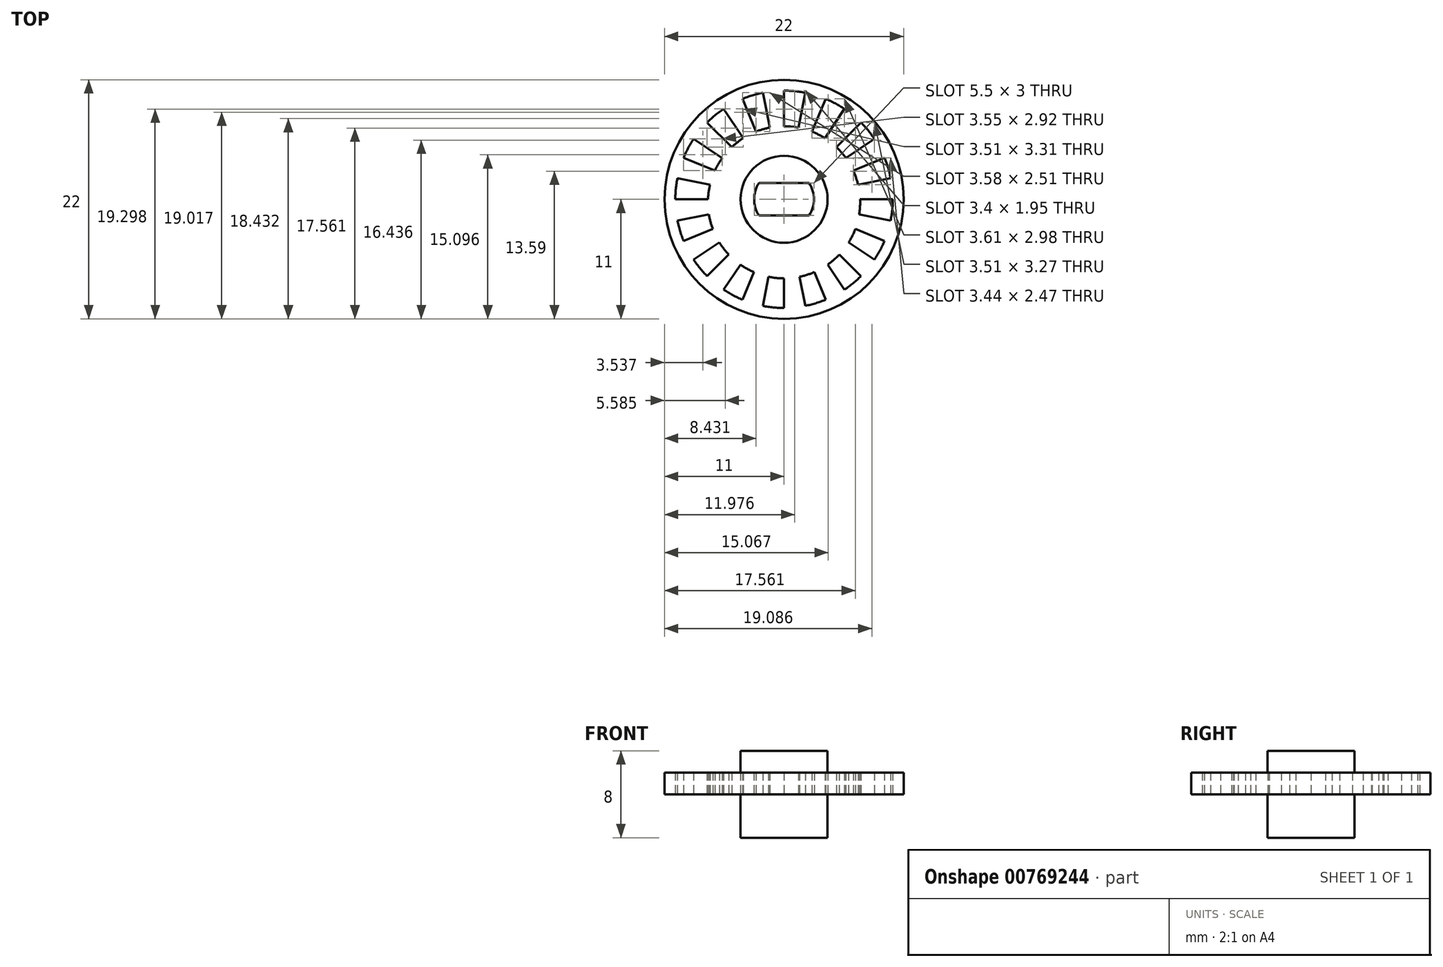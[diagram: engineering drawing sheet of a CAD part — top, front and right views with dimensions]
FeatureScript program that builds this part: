
annotation { "Feature Type Name" : "Feature", "Feature Type Description" : "" }
export const myFeature = defineFeature(function(context is Context, id is Id, definition is map)
    precondition{}
    {
        {
            var Q0;
            Q0=qCreatedBy(makeId("Top.planeOp"),FACE);
            var sketch = newSketch(context, id + "F0", { "sketchPlane" : qUnion([Q0])});
            skCircle(sketch, "E0", {"center": v(0, 0) * mm, "radius": 11 * mm});
            skArc(sketch, "E1", {"start": v(-2.3, 1.5) * mm, "mid": v(-2.75, 0) * mm, "end": v(-2.3, -1.5) * mm});
            skCircle(sketch, "E2", {"center": v(0, 0) * mm, "radius": 4 * mm});
            skLineSegment(sketch, "E3.bottom", {"start": v(-2.3, 1.5) * mm, "end": v(2.3, 1.5) * mm});
            skLineSegment(sketch, "E3.top", {"start": v(-2.3, -1.5) * mm, "end": v(2.3, -1.5) * mm});
            skArc(sketch, "E4.trimOffspring", {"start": v(2.3, -1.5) * mm, "mid": v(2.75, 0) * mm, "end": v(2.3, 1.5) * mm});
            skArc(sketch, "E5", {"start": v(-1.95, -9.8) * mm, "mid": v(-0.98, -9.95) * mm, "end": v(0, -10) * mm});
            skLineSegment(sketch, "E6.trimOffspring", {"start": v(0, -7.28) * mm, "end": v(0, -10) * mm});
            skLineSegment(sketch, "E7.1.0", {"start": v(1.42, -7.14) * mm, "end": v(1.95, -9.8) * mm});
            skLineSegment(sketch, "E7.2.0", {"start": v(2.78, -6.7) * mm, "end": v(3.83, -9.24) * mm});
            skLineSegment(sketch, "E7.3.0", {"start": v(4.02, -6.01) * mm, "end": v(5.56, -8.31) * mm});
            skLineSegment(sketch, "E7.4.0", {"start": v(5.09, -5.09) * mm, "end": v(7.07, -7.07) * mm});
            skLineSegment(sketch, "E7.5.0", {"start": v(5.95, -3.97) * mm, "end": v(8.31, -5.56) * mm});
            skLineSegment(sketch, "E7.6.0", {"start": v(6.56, -2.72) * mm, "end": v(9.24, -3.83) * mm});
            skLineSegment(sketch, "E7.7.0", {"start": v(6.91, -1.38) * mm, "end": v(9.8, -1.95) * mm});
            skLineSegment(sketch, "E7.8.0", {"start": v(7, 0) * mm, "end": v(10, 0) * mm});
            skLineSegment(sketch, "E7.9.0", {"start": v(6.8, 1.35) * mm, "end": v(9.8, 1.95) * mm});
            skLineSegment(sketch, "E7.10.0", {"start": v(6.36, 2.64) * mm, "end": v(9.24, 3.83) * mm});
            skLineSegment(sketch, "E7.11.0", {"start": v(5.69, 3.8) * mm, "end": v(8.31, 5.56) * mm});
            skLineSegment(sketch, "E7.12.0", {"start": v(4.8, 4.8) * mm, "end": v(7.07, 7.07) * mm});
            skLineSegment(sketch, "E7.13.0", {"start": v(3.76, 5.62) * mm, "end": v(5.56, 8.31) * mm});
            skLineSegment(sketch, "E7.14.0", {"start": v(2.58, 6.23) * mm, "end": v(3.83, 9.24) * mm});
            skLineSegment(sketch, "E7.15.0", {"start": v(1.31, 6.6) * mm, "end": v(1.95, 9.8) * mm});
            skLineSegment(sketch, "E7.16.0", {"start": v(0, 6.72) * mm, "end": v(0, 10) * mm});
            skLineSegment(sketch, "E7.17.0", {"start": v(-1.31, 6.6) * mm, "end": v(-1.95, 9.8) * mm});
            skLineSegment(sketch, "E7.18.0", {"start": v(-2.58, 6.23) * mm, "end": v(-3.83, 9.24) * mm});
            skLineSegment(sketch, "E7.19.0", {"start": v(-3.76, 5.62) * mm, "end": v(-5.56, 8.31) * mm});
            skLineSegment(sketch, "E7.20.0", {"start": v(-4.8, 4.8) * mm, "end": v(-7.07, 7.07) * mm});
            skLineSegment(sketch, "E7.21.0", {"start": v(-5.69, 3.8) * mm, "end": v(-8.31, 5.56) * mm});
            skLineSegment(sketch, "E7.22.0", {"start": v(-6.36, 2.64) * mm, "end": v(-9.24, 3.83) * mm});
            skLineSegment(sketch, "E7.23.0", {"start": v(-6.8, 1.35) * mm, "end": v(-9.8, 1.95) * mm});
            skLineSegment(sketch, "E7.24.0", {"start": v(-7, 0) * mm, "end": v(-10, 0) * mm});
            skLineSegment(sketch, "E7.25.0", {"start": v(-6.91, -1.38) * mm, "end": v(-9.8, -1.95) * mm});
            skLineSegment(sketch, "E7.26.0", {"start": v(-6.56, -2.72) * mm, "end": v(-9.24, -3.83) * mm});
            skLineSegment(sketch, "E7.27.0", {"start": v(-5.95, -3.97) * mm, "end": v(-8.31, -5.56) * mm});
            skLineSegment(sketch, "E7.28.0", {"start": v(-5.09, -5.09) * mm, "end": v(-7.07, -7.07) * mm});
            skLineSegment(sketch, "E7.29.0", {"start": v(-4.02, -6.01) * mm, "end": v(-5.56, -8.31) * mm});
            skLineSegment(sketch, "E7.30.0", {"start": v(-2.78, -6.7) * mm, "end": v(-3.83, -9.24) * mm});
            skLineSegment(sketch, "E7.31.0", {"start": v(-1.42, -7.14) * mm, "end": v(-1.95, -9.8) * mm});
            skArc(sketch, "E8.trimOffspring", {"start": v(-5.56, -8.31) * mm, "mid": v(-4.71, -8.82) * mm, "end": v(-3.83, -9.24) * mm});
            skArc(sketch, "E9.trimOffspring", {"start": v(-8.31, -5.56) * mm, "mid": v(-7.73, -6.34) * mm, "end": v(-7.07, -7.07) * mm});
            skArc(sketch, "E10.trimOffspring", {"start": v(-9.8, -1.95) * mm, "mid": v(-9.57, -2.9) * mm, "end": v(-9.24, -3.83) * mm});
            skArc(sketch, "E11.trimOffspring", {"start": v(-9.8, 1.95) * mm, "mid": v(-9.95, 0.98) * mm, "end": v(-10, 0) * mm});
            skArc(sketch, "E12.trimOffspring", {"start": v(-8.31, 5.56) * mm, "mid": v(-8.82, 4.71) * mm, "end": v(-9.24, 3.83) * mm});
            skArc(sketch, "E13.trimOffspring", {"start": v(-5.56, 8.31) * mm, "mid": v(-6.34, 7.73) * mm, "end": v(-7.07, 7.07) * mm});
            skArc(sketch, "E14.trimOffspring", {"start": v(-1.95, 9.8) * mm, "mid": v(-2.9, 9.57) * mm, "end": v(-3.83, 9.24) * mm});
            skArc(sketch, "E15.trimOffspring", {"start": v(1.95, 9.8) * mm, "mid": v(0.98, 9.95) * mm, "end": v(0, 10) * mm});
            skArc(sketch, "E16.trimOffspring", {"start": v(5.56, 8.31) * mm, "mid": v(4.71, 8.82) * mm, "end": v(3.83, 9.24) * mm});
            skArc(sketch, "E17.trimOffspring", {"start": v(8.31, 5.56) * mm, "mid": v(7.73, 6.34) * mm, "end": v(7.07, 7.07) * mm});
            skArc(sketch, "E18.trimOffspring", {"start": v(9.8, 1.95) * mm, "mid": v(9.57, 2.9) * mm, "end": v(9.24, 3.83) * mm});
            skArc(sketch, "E19.trimOffspring", {"start": v(9.8, -1.95) * mm, "mid": v(9.95, -0.98) * mm, "end": v(10, 0) * mm});
            skArc(sketch, "E20.trimOffspring", {"start": v(5.56, -8.31) * mm, "mid": v(6.34, -7.73) * mm, "end": v(7.07, -7.07) * mm});
            skArc(sketch, "E21.trimOffspring", {"start": v(8.31, -5.56) * mm, "mid": v(8.82, -4.71) * mm, "end": v(9.24, -3.83) * mm});
            skArc(sketch, "E22.trimOffspring", {"start": v(1.95, -9.8) * mm, "mid": v(2.9, -9.57) * mm, "end": v(3.83, -9.24) * mm});
            skArc(sketch, "E23", {"start": v(-6.91, -1.38) * mm, "mid": v(-6.77, -2.06) * mm, "end": v(-6.56, -2.72) * mm});
            skArc(sketch, "E24.trimOffspring", {"start": v(-6.8, 1.35) * mm, "mid": v(-6.93, 0.68) * mm, "end": v(-7, 0) * mm});
            skArc(sketch, "E25.trimOffspring", {"start": v(-5.69, 3.8) * mm, "mid": v(-6.05, 3.23) * mm, "end": v(-6.36, 2.64) * mm});
            skArc(sketch, "E26.trimOffspring", {"start": v(-3.76, 5.62) * mm, "mid": v(-4.3, 5.24) * mm, "end": v(-4.8, 4.8) * mm});
            skArc(sketch, "E27.trimOffspring", {"start": v(-1.31, 6.6) * mm, "mid": v(-1.95, 6.44) * mm, "end": v(-2.58, 6.23) * mm});
            skArc(sketch, "E28.trimOffspring", {"start": v(1.31, 6.6) * mm, "mid": v(0.66, 6.69) * mm, "end": v(0, 6.72) * mm});
            skArc(sketch, "E29.trimOffspring", {"start": v(3.76, 5.62) * mm, "mid": v(3.18, 5.95) * mm, "end": v(2.58, 6.23) * mm});
            skArc(sketch, "E30.trimOffspring", {"start": v(5.69, 3.8) * mm, "mid": v(5.27, 4.32) * mm, "end": v(4.8, 4.8) * mm});
            skArc(sketch, "E31.trimOffspring", {"start": v(6.8, 1.35) * mm, "mid": v(6.62, 2) * mm, "end": v(6.36, 2.64) * mm});
            skArc(sketch, "E32.trimOffspring", {"start": v(6.91, -1.38) * mm, "mid": v(6.99, -0.69) * mm, "end": v(7, 0) * mm});
            skArc(sketch, "E33.trimOffspring", {"start": v(5.95, -3.97) * mm, "mid": v(6.29, -3.36) * mm, "end": v(6.56, -2.72) * mm});
            skArc(sketch, "E34.trimOffspring", {"start": v(4.02, -6.01) * mm, "mid": v(4.58, -5.58) * mm, "end": v(5.09, -5.09) * mm});
            skArc(sketch, "E35.trimOffspring", {"start": v(1.42, -7.14) * mm, "mid": v(2.1, -6.96) * mm, "end": v(2.78, -6.7) * mm});
            skArc(sketch, "E36.trimOffspring", {"start": v(-1.42, -7.14) * mm, "mid": v(-0.71, -7.24) * mm, "end": v(0, -7.28) * mm});
            skArc(sketch, "E37.trimOffspring", {"start": v(-4.02, -6.01) * mm, "mid": v(-3.42, -6.4) * mm, "end": v(-2.78, -6.7) * mm});
            skArc(sketch, "E38.trimOffspring", {"start": v(-5.95, -3.97) * mm, "mid": v(-5.55, -4.55) * mm, "end": v(-5.09, -5.09) * mm});
            skSolve(sketch);
        }
        {
            var Q0;
            Q0=makeQuery(id+"F0.imprint","IMPRINT",FACE,{"disambiguationData":[TD([[makeQuery(id+"F0.imprint","IMPRINT",EDGE,{"derivedFrom":sQuery(id+"F0.wireOp",EDGE,"E1")}),-1.0]])]});
            extrude(context, id + "F1", {"entities" : qUnion([Q0]), "endBound" : BoundingType.SYMMETRIC, "depth" : 8 * mm, "offsetDistance" : 25 * mm});
        }
        {
            var Q0;
            Q0=makeQuery(id+"F0.imprint","IMPRINT",FACE,{"disambiguationData":[TD([[makeQuery(id+"F0.imprint","IMPRINT",EDGE,{"derivedFrom":sQuery(id+"F0.wireOp",EDGE,"E0")}),1.0]])]});
            extrude(context, id + "F2", {"entities" : qUnion([Q0]), "operationType" : NewBodyOperationType.ADD, "depth" : 2 * mm, "offsetDistance" : 25 * mm});
        }
    });
